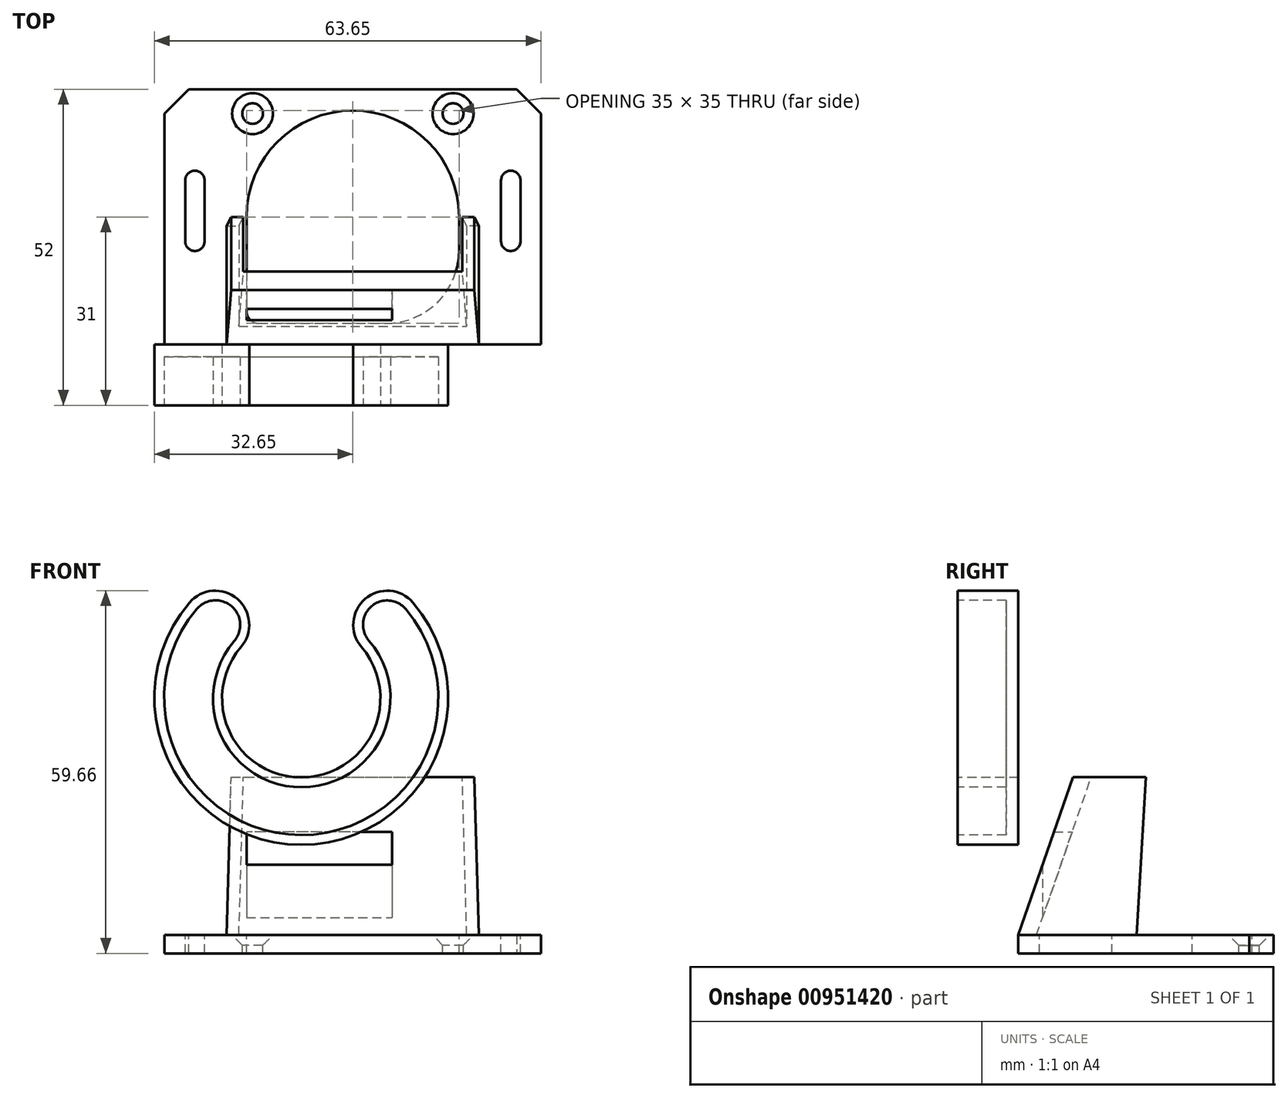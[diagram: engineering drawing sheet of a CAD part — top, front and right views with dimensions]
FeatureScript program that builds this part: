
annotation { "Feature Type Name" : "Feature", "Feature Type Description" : "" }
export const myFeature = defineFeature(function(context is Context, id is Id, definition is map)
    precondition{}
    {
        {
            var Q0;
            Q0=qCreatedBy(makeId("Top.planeOp"),FACE);
            var sketch = newSketch(context, id + "F0", { "sketchPlane" : qUnion([Q0])});
            skLineSegment(sketch, "E0.bottom", {"start": v(-31, 21) * mm, "end": v(31, 21) * mm});
            skLineSegment(sketch, "E0.top", {"start": v(-21, -21) * mm, "end": v(21.02, -21) * mm});
            skLineSegment(sketch, "E0.left", {"start": v(-31, 21) * mm, "end": v(-31, -9) * mm});
            skLineSegment(sketch, "E0.right", {"start": v(31, 21) * mm, "end": v(31, -9) * mm});
            skPoint(sketch, "E0.middle", {"position": v(0, 0) * mm});
            skLineSegment(sketch, "E1", {"start": v(-17.5, 0) * mm, "end": v(17.5, 0) * mm, "construction": true});
            skLineSegment(sketch, "E2.0", {"start": v(26, 21) * mm, "end": v(26, -21) * mm, "construction": true});
            skLineSegment(sketch, "E3.0", {"start": v(-26, 21) * mm, "end": v(-26, -21) * mm, "construction": true});
            skLineSegment(sketch, "E4.bottom", {"start": v(-27.6, -4) * mm, "end": v(-24.4, -4) * mm});
            skLineSegment(sketch, "E4.top", {"start": v(-27.6, 6) * mm, "end": v(-24.4, 6) * mm});
            skLineSegment(sketch, "E4.left", {"start": v(-27.6, -4) * mm, "end": v(-27.6, 6) * mm});
            skLineSegment(sketch, "E4.right", {"start": v(-24.4, -4) * mm, "end": v(-24.4, 6) * mm});
            skPoint(sketch, "E4.middle", {"position": v(-26, 1) * mm});
            skLineSegment(sketch, "E5.bottom", {"start": v(24.4, -4) * mm, "end": v(27.6, -4) * mm, "construction": true});
            skLineSegment(sketch, "E5.top", {"start": v(24.4, 6) * mm, "end": v(27.6, 6) * mm, "construction": true});
            skLineSegment(sketch, "E5.left", {"start": v(24.4, -4) * mm, "end": v(24.4, 6) * mm});
            skLineSegment(sketch, "E5.right", {"start": v(27.6, -4) * mm, "end": v(27.6, 6) * mm});
            skPoint(sketch, "E5.middle", {"position": v(26, 1) * mm});
            skArc(sketch, "E6", {"start": v(27.6, 6) * mm, "mid": v(26, 7.6) * mm, "end": v(24.4, 6) * mm});
            skArc(sketch, "E7", {"start": v(24.4, -4) * mm, "mid": v(26, -5.6) * mm, "end": v(27.6, -4) * mm});
            skArc(sketch, "E8", {"start": v(-27.6, -4) * mm, "mid": v(-26, -5.6) * mm, "end": v(-24.4, -4) * mm});
            skArc(sketch, "E9", {"start": v(-24.4, 6) * mm, "mid": v(-26, 7.6) * mm, "end": v(-27.6, 6) * mm});
            skLineSegment(sketch, "E10", {"start": v(31, -9) * mm, "end": v(21.02, -9) * mm});
            skLineSegment(sketch, "E11", {"start": v(-31, -9) * mm, "end": v(-21, -9) * mm});
            skLineSegment(sketch, "E12", {"start": v(-21, -9) * mm, "end": v(-21, -21) * mm});
            skLineSegment(sketch, "E13", {"start": v(21.02, -9) * mm, "end": v(21.02, -21) * mm});
            skPoint(sketch, "E14.orphan", {"position": v(-31, -21) * mm});
            skPoint(sketch, "E15.trimOffspring.end.orphan", {"position": v(31, -21) * mm});
            skPoint(sketch, "E16", {"position": v(-16.5, 17) * mm});
            skPoint(sketch, "E17", {"position": v(16.5, 17) * mm});
            skLineSegment(sketch, "E18", {"start": v(0, 28) * mm, "end": v(0, -24.83) * mm, "construction": true});
            skArc(sketch, "E19.trimOffspring", {"start": v(17.5, 0) * mm, "mid": v(0, 17.5) * mm, "end": v(-17.5, 0) * mm});
            skLineSegment(sketch, "E20", {"start": v(21.02, -21) * mm, "end": v(31, -21) * mm});
            skLineSegment(sketch, "E21", {"start": v(31, -21) * mm, "end": v(31, -9) * mm});
            skLineSegment(sketch, "E22", {"start": v(-31, -9) * mm, "end": v(-31, -21) * mm});
            skLineSegment(sketch, "E23", {"start": v(-31, -21) * mm, "end": v(-21, -21) * mm});
            skLineSegment(sketch, "E24", {"start": v(-17.5, 0) * mm, "end": v(-17.5, -15.5) * mm});
            skPoint(sketch, "E24.endSnap0", {"position": v(-1.48, -17.5) * mm});
            skLineSegment(sketch, "E25", {"start": v(-15.5, -17.5) * mm, "end": v(5.5, -17.5) * mm});
            skLineSegment(sketch, "E26", {"start": v(17.5, -5.5) * mm, "end": v(17.5, 0) * mm});
            skPoint(sketch, "E27.visualSharp", {"position": v(-17.5, -17.5) * mm});
            skArc(sketch, "E27.filletArc", {"start": v(-17.5, -15.5) * mm, "mid": v(-16.91, -16.91) * mm, "end": v(-15.5, -17.5) * mm});
            skPoint(sketch, "E28.visualSharp", {"position": v(17.5, -17.5) * mm});
            skArc(sketch, "E28.filletArc", {"start": v(5.5, -17.5) * mm, "mid": v(13.99, -13.99) * mm, "end": v(17.5, -5.5) * mm});
            skSolve(sketch);
        }
        {
            var Q0;
            Q0=makeQuery(id+"F0.imprint","IMPRINT",FACE,{"disambiguationData":[TD([[makeQuery(id+"F0.imprint","IMPRINT",EDGE,{"derivedFrom":sQuery(id+"F0.wireOp",EDGE,"zgBuKsxa-OEMX-4A7b-Va0U-zt6h8Rh99ESV")}),-1.0]])]});
            var Q1;
            Q1=makeQuery(id+"F0.imprint","IMPRINT",FACE,{"disambiguationData":[TD([[makeQuery(id+"F0.imprint","IMPRINT",EDGE,{"derivedFrom":sQuery(id+"F0.wireOp",EDGE,"E11")}),-1.0]])]});
            var Q2;
            Q2=makeQuery(id+"F0.imprint","IMPRINT",FACE,{"disambiguationData":[TD([[makeQuery(id+"F0.imprint","IMPRINT",EDGE,{"derivedFrom":sQuery(id+"F0.wireOp",EDGE,"E10")}),1.0]])]});
            var Q3;
            Q3=makeQuery(id+"F0.imprint","IMPRINT",FACE,{"disambiguationData":[TD([[makeQuery(id+"F0.imprint","IMPRINT",EDGE,{"derivedFrom":sQuery(id+"F0.wireOp",EDGE,"E0.bottom")}),-1.0]])]});
            extrude(context, id + "F1", {"entities" : qUnion([Q0, Q1, Q2, Q3]), "oppositeDirection" : true, "depth" : 3 * mm, "offsetDistance" : 25 * mm});
        }
        {
            var Q0;
            Q0=sQuery(id+"F0.wireOp",VERTEX,"E16");
            var Q1;
            Q1=sQuery(id+"F0.wireOp",VERTEX,"E17");
            var Q2;
            Q2=makeQuery(id+"F1.opExtrude","SWEPT_BODY",BODY,{"disambiguationData":[OSD([sQuery(id+"F0.wireOp",EDGE,"zgBuKsxa-OEMX-4A7b-Va0U-zt6h8Rh99ESV"),sQuery(id+"F0.wireOp",EDGE,"E0.bottom"),sQuery(id+"F0.wireOp",EDGE,"E0.top"),sQuery(id+"F0.wireOp",EDGE,"E0.left"),sQuery(id+"F0.wireOp",EDGE,"E0.right"),sQuery(id+"F0.wireOp",EDGE,"8023575a-cc51-4947-99a3-caa3ee00ee31.0"),sQuery(id+"F0.wireOp",EDGE,"259734f9-b8b1-401e-8cfd-9bb92d609301.0"),sQuery(id+"F0.wireOp",EDGE,"E4.left"),sQuery(id+"F0.wireOp",EDGE,"E4.right"),sQuery(id+"F0.wireOp",EDGE,"E5.left"),sQuery(id+"F0.wireOp",EDGE,"E5.right"),sQuery(id+"F0.wireOp",EDGE,"E6"),sQuery(id+"F0.wireOp",EDGE,"E7"),sQuery(id+"F0.wireOp",EDGE,"E8"),sQuery(id+"F0.wireOp",EDGE,"E9"),sQuery(id+"F0.wireOp",EDGE,"E10"),sQuery(id+"F0.wireOp",EDGE,"E11"),sQuery(id+"F0.wireOp",EDGE,"E12"),sQuery(id+"F0.wireOp",EDGE,"E13"),sQuery(id+"F0.wireOp",EDGE,"E19.trimOffspring")])]});
            hole(context, id + "F2", {"style" : HoleStyle.C_SINK, "endStyle" : HoleEndStyle.THROUGH, "standardTappedOrClearance" : lookupTablePath({ "fit" : "Normal", "standard" : "ISO", "size" : "M3", "type" : "Clearance" }), "standardBlindInLast" : lookupTablePath({ "fit" : "Normal", "standard" : "ISO", "engagement" : "75%", "pitch" : "0.5 mm", "size" : "M3", "type" : "Clearance & tapped" }), "holeDiameter" : 3.4 * mm, "cSinkDiameter" : 6.72 * mm, "cSinkAngle" : 90 * degree, "majorDiameter" : 5 * mm, "isTappedThrough" : true, "tappedDepth" : 12 * mm, "tapClearance" : 3, "locations" : qUnion([Q0, Q1]), "scope" : qUnion([Q2])});
        }
        {
            var Q0;
            Q0=makeQuery(id+"F1.opExtrude","SWEPT_EDGE",EDGE,{"disambiguationData":[OSD([sQuery(id+"F0.wireOp",EDGE,"E0.bottom"),sQuery(id+"F0.wireOp",EDGE,"E0.right")])]});
            var Q1;
            Q1=makeQuery(id+"F1.opExtrude","SWEPT_EDGE",EDGE,{"disambiguationData":[OSD([sQuery(id+"F0.wireOp",EDGE,"E0.bottom"),sQuery(id+"F0.wireOp",EDGE,"E0.left")])]});
            chamfer(context, id + "F3", {"entities" : qUnion([Q0, Q1]), "width" : 4 * mm, "tangentPropagation" : true});
        }
        {
            var Q0;
            Q0=makeQuery(id+"F1.opExtrude","CAP_FACE",FACE,{"disambiguationData":[OSD([sQuery(id+"F0.wireOp",EDGE,"zgBuKsxa-OEMX-4A7b-Va0U-zt6h8Rh99ESV"),sQuery(id+"F0.wireOp",EDGE,"E0.bottom"),sQuery(id+"F0.wireOp",EDGE,"E0.top"),sQuery(id+"F0.wireOp",EDGE,"E0.left"),sQuery(id+"F0.wireOp",EDGE,"E0.right"),sQuery(id+"F0.wireOp",EDGE,"8023575a-cc51-4947-99a3-caa3ee00ee31.0"),sQuery(id+"F0.wireOp",EDGE,"259734f9-b8b1-401e-8cfd-9bb92d609301.0"),sQuery(id+"F0.wireOp",EDGE,"E4.left"),sQuery(id+"F0.wireOp",EDGE,"E4.right"),sQuery(id+"F0.wireOp",EDGE,"E5.left"),sQuery(id+"F0.wireOp",EDGE,"E5.right"),sQuery(id+"F0.wireOp",EDGE,"E6"),sQuery(id+"F0.wireOp",EDGE,"E7"),sQuery(id+"F0.wireOp",EDGE,"E8"),sQuery(id+"F0.wireOp",EDGE,"E9"),sQuery(id+"F0.wireOp",EDGE,"E10"),sQuery(id+"F0.wireOp",EDGE,"E11"),sQuery(id+"F0.wireOp",EDGE,"E12"),sQuery(id+"F0.wireOp",EDGE,"E13"),sQuery(id+"F0.wireOp",EDGE,"E19.trimOffspring")])],"isStart":true});
            var sketch = newSketch(context, id + "F4", { "sketchPlane" : qUnion([Q0])});
            skLineSegment(sketch, "E29.0", {"start": v(-20.75, -1.5) * mm, "end": v(-20.75, -21) * mm});
            skLineSegment(sketch, "E30.0", {"start": v(-20.75, -21) * mm, "end": v(20.75, -21) * mm});
            skLineSegment(sketch, "E31.0", {"start": v(20.75, -1.5) * mm, "end": v(20.75, -21) * mm});
            skLineSegment(sketch, "E32.0", {"start": v(18.75, -1.5) * mm, "end": v(18.75, -18) * mm});
            skLineSegment(sketch, "E32.1", {"start": v(-18.75, -18) * mm, "end": v(18.75, -18) * mm});
            skLineSegment(sketch, "E32.2", {"start": v(-18.75, -1.5) * mm, "end": v(-18.75, -18) * mm});
            skLineSegment(sketch, "E33", {"start": v(-20.75, -1.5) * mm, "end": v(-18.75, -1.5) * mm});
            skLineSegment(sketch, "E34", {"start": v(20.75, -1.5) * mm, "end": v(18.75, -1.5) * mm});
            skLineSegment(sketch, "E35", {"start": v(0, 24.47) * mm, "end": v(0, -25.01) * mm, "construction": true});
            skSolve(sketch);
        }
        {
            var Q0;
            Q0=makeQuery(id+"F4.imprint","IMPRINT",FACE,{"disambiguationData":[TD([[makeQuery(id+"F4.imprint","IMPRINT",EDGE,{"derivedFrom":sQuery(id+"F4.wireOp",EDGE,"E32.0")}),-1.0]])]});
            cPlane(context, id + "F5", {"entities" : qUnion([Q0]), "cplaneType" : CPlaneType.OFFSET, "offset" : 26 * mm, "width" : 150 * mm, "height" : 150 * mm});
        }
        {
            var Q0;
            Q0=qCreatedBy(id+"F5.planeOp",FACE);
            var sketch = newSketch(context, id + "F6", { "sketchPlane" : qUnion([Q0])});
            skLineSegment(sketch, "E36", {"start": v(-20.02, -12) * mm, "end": v(-20.02, 0) * mm});
            skLineSegment(sketch, "E37", {"start": v(20.02, -12) * mm, "end": v(20.02, 0) * mm});
            skLineSegment(sketch, "E38", {"start": v(20.02, 0) * mm, "end": v(18.02, 0) * mm});
            skLineSegment(sketch, "E39", {"start": v(18.02, 0) * mm, "end": v(18.02, -9) * mm});
            skLineSegment(sketch, "E40", {"start": v(-20.02, 0) * mm, "end": v(-18.02, 0) * mm});
            skLineSegment(sketch, "E41", {"start": v(-18.02, 0) * mm, "end": v(-18.02, -9) * mm});
            skLineSegment(sketch, "E42", {"start": v(-18.02, -9) * mm, "end": v(18.02, -9) * mm});
            skLineSegment(sketch, "E43", {"start": v(-20.02, -12) * mm, "end": v(20.02, -12) * mm});
            skSolve(sketch);
        }
        {
            var Q1;
            Q1=qSketchRegion(id+"F4",true);
            var Q2;
            Q2=qSketchRegion(id+"F6",true);
            loft(context, id + "F7", {"operationType" : NewBodyOperationType.ADD, "sheetProfilesArray" : [{ "sheetProfileEntities" : qUnion([Q1]) }, { "sheetProfileEntities" : qUnion([Q2]) }]});
        }
        {
            var Q0;
            Q0=makeQuery(id+"F1.opExtrude","CAP_FACE",FACE,{"disambiguationData":[OSD([sQuery(id+"F0.wireOp",EDGE,"zgBuKsxa-OEMX-4A7b-Va0U-zt6h8Rh99ESV"),sQuery(id+"F0.wireOp",EDGE,"E0.bottom"),sQuery(id+"F0.wireOp",EDGE,"E0.top"),sQuery(id+"F0.wireOp",EDGE,"E0.left"),sQuery(id+"F0.wireOp",EDGE,"E0.right"),sQuery(id+"F0.wireOp",EDGE,"E4.left"),sQuery(id+"F0.wireOp",EDGE,"E4.right"),sQuery(id+"F0.wireOp",EDGE,"E5.left"),sQuery(id+"F0.wireOp",EDGE,"E5.right"),sQuery(id+"F0.wireOp",EDGE,"E6"),sQuery(id+"F0.wireOp",EDGE,"E7"),sQuery(id+"F0.wireOp",EDGE,"E8"),sQuery(id+"F0.wireOp",EDGE,"E9"),sQuery(id+"F0.wireOp",EDGE,"E19.trimOffspring"),sQuery(id+"F0.wireOp",EDGE,"E20"),sQuery(id+"F0.wireOp",EDGE,"E21"),sQuery(id+"F0.wireOp",EDGE,"E22"),sQuery(id+"F0.wireOp",EDGE,"E23")])],"isStart":true});
            cPlane(context, id + "F8", {"entities" : qUnion([Q0]), "cplaneType" : CPlaneType.OFFSET, "offset" : 2 * mm, "width" : 150 * mm, "height" : 150 * mm});
        }
        {
            var Q0;
            Q0=qCreatedBy(id+"F8.planeOp",FACE);
            var sketch = newSketch(context, id + "F9", { "sketchPlane" : qUnion([Q0])});
            skLineSegment(sketch, "E44.bottom", {"start": v(6.5, -17) * mm, "end": v(-17.5, -17) * mm});
            skLineSegment(sketch, "E44.top", {"start": v(6.5, -12) * mm, "end": v(-17.5, -12) * mm});
            skLineSegment(sketch, "E44.left", {"start": v(6.5, -17) * mm, "end": v(6.5, -12) * mm});
            skLineSegment(sketch, "E44.right", {"start": v(-17.5, -17) * mm, "end": v(-17.5, -12) * mm});
            skSolve(sketch);
        }
        {
            var Q0;
            Q0=makeQuery(id+"F9.imprint","IMPRINT",FACE,{"disambiguationData":[TD([[makeQuery(id+"F9.imprint","IMPRINT",EDGE,{"derivedFrom":sQuery(id+"F9.wireOp",EDGE,"E44.bottom")}),-1.0]])]});
            extrude(context, id + "F10", {"entities" : qUnion([Q0]), "operationType" : NewBodyOperationType.REMOVE, "depth" : 15 * mm, "offsetDistance" : 25 * mm});
        }
        {
            var Q0;
            Q0=makeQuery(id+"F7.opLoft","SWEPT_FACE",FACE,{"disambiguationData":[OSD([sQuery(id+"F0.wireOp",EDGE,"E0.top"),sQuery(id+"F0.wireOp",EDGE,"E20"),sQuery(id+"F0.wireOp",EDGE,"E23"),sQuery(id+"F4.wireOp",EDGE,"E29.0"),sQuery(id+"F4.wireOp",EDGE,"E30.0"),sQuery(id+"F4.wireOp",EDGE,"E31.0"),sQuery(id+"F6.wireOp",EDGE,"E36"),sQuery(id+"F6.wireOp",EDGE,"E37"),sQuery(id+"F6.wireOp",EDGE,"E43")])]});
            var sketch = newSketch(context, id + "F11", { "sketchPlane" : qUnion([Q0])});
            skLineSegment(sketch, "E45.0", {"start": v(6.5, 11.12) * mm, "end": v(-17.5, 11.12) * mm, "construction": true});
            skLineSegment(sketch, "E46.0", {"start": v(-17.5, 11.12) * mm, "end": v(-17.5, 5.36) * mm, "construction": true});
            skEllipse(sketch, "E47", {"center": v(-5.5, 8.24) * mm, "majorRadius": 13.18 * mm, "minorRadius": 6.7 * mm, "majorAxis": v(1, 0)});
            skPoint(sketch, "E47.centerSnap0", {"position": v(-17.5, 8.24) * mm});
            skPoint(sketch, "E47.centerSnap1", {"position": v(-5.5, 11.12) * mm});
            skFitSpline(sketch, "E48.0", {"points": [v(9.22, 13.3) * mm, v(9.31, 14.28) * mm, v(9.22, 15.25) * mm, v(8.85, 16.5) * mm, v(8.17, 17.62) * mm, v(7.25, 18.6) * mm, v(6.17, 19.52) * mm, v(4.6, 20.49) * mm, v(2.76, 21.26) * mm, v(1.14, 21.75) * mm, v(-0.54, 22.15) * mm, v(-2.3, 22.43) * mm, v(-4.12, 22.56) * mm, v(-5.5, 22.6) * mm, v(-6.88, 22.56) * mm, v(-8.7, 22.43) * mm, v(-10.46, 22.15) * mm, v(-12.14, 21.75) * mm, v(-13.76, 21.26) * mm, v(-15.6, 20.49) * mm, v(-17.17, 19.52) * mm, v(-18.25, 18.6) * mm, v(-19.17, 17.62) * mm, v(-19.85, 16.5) * mm, v(-20.22, 15.25) * mm, v(-20.31, 14.28) * mm, v(-20.22, 13.3) * mm, v(-19.85, 12.06) * mm, v(-19.17, 10.94) * mm, v(-18.25, 9.95) * mm, v(-17.17, 9.04) * mm, v(-15.6, 8.07) * mm, v(-13.76, 7.3) * mm, v(-12.14, 6.8) * mm, v(-10.46, 6.4) * mm, v(-8.7, 6.13) * mm, v(-6.88, 6) * mm, v(-5.5, 5.96) * mm, v(-4.12, 6) * mm, v(-2.3, 6.13) * mm, v(-0.54, 6.4) * mm, v(1.14, 6.8) * mm, v(2.76, 7.3) * mm, v(4.6, 8.07) * mm, v(6.17, 9.04) * mm, v(7.25, 9.95) * mm, v(8.17, 10.94) * mm, v(8.85, 12.06) * mm, v(9.22, 13.3) * mm, v(9.31, 14.28) * mm, v(9.22, 15.25) * mm, v(9.22, 13.3) * mm]});
            skSolve(sketch);
        }
        {
            var Q0;
            {var subQ0=sQuery(id+"F0.wireOp",EDGE,"E23");var subQ1=sQuery(id+"F0.wireOp",EDGE,"E20");var subQ2=sQuery(id+"F0.wireOp",EDGE,"E0.top");Q0=makeQuery(id+"FMINiw3eGN9fXnE_1.boolean.opBoolean","SPLIT",FACE,{"disambiguationData":[TD([makeQuery(id+"FMINiw3eGN9fXnE_1.opExtrude","SWEPT_FACE",FACE,{"disambiguationData":[OSD([sQuery(id+"Far563bkZVvMWru_1.wireOp",EDGE,"df4eb139-c0bc-4f98-82ec-923183797030.0")])]})])],"derivedFrom":makeQuery(id+"F1.opExtrude","SWEPT_FACE",FACE,{"disambiguationData":[OSD([subQ2,subQ1,subQ0])]})});}
            cPlane(context, id + "F12", {"entities" : qUnion([Q0]), "cplaneType" : CPlaneType.OFFSET, "offset" : 10 * mm, "width" : 150 * mm, "height" : 150 * mm});
        }
        {
            var Q0;
            Q0=qCreatedBy(id+"F12.planeOp",FACE);
            var sketch = newSketch(context, id + "F13", { "sketchPlane" : qUnion([Q0])});
            skLineSegment(sketch, "E49.0", {"start": v(13.92, 49) * mm, "end": v(11.52, 49) * mm, "construction": true});
            skLineSegment(sketch, "E49.1", {"start": v(13.92, 49) * mm, "end": v(13.92, 25.6) * mm, "construction": true});
            skLineSegment(sketch, "E49.4", {"start": v(-24.88, 49) * mm, "end": v(-24.88, 25.6) * mm, "construction": true});
            skLineSegment(sketch, "E49.5", {"start": v(10.52, 50) * mm, "end": v(10.52, 29) * mm, "construction": true});
            skLineSegment(sketch, "E49.7", {"start": v(10.52, 29) * mm, "end": v(-21.48, 29) * mm, "construction": true});
            skLineSegment(sketch, "E49.9", {"start": v(-21.48, 50) * mm, "end": v(-21.48, 29) * mm, "construction": true});
            skLineSegment(sketch, "E49.10", {"start": v(-22.48, 49) * mm, "end": v(-24.88, 49) * mm, "construction": true});
            skPoint(sketch, "E50.visualSharp", {"position": v(13.92, 25.6) * mm});
            skLineSegment(sketch, "E51", {"start": v(-21.48, 49) * mm, "end": v(10.52, 49) * mm, "construction": true});
            skLineSegment(sketch, "E52.0", {"start": v(-20.75, 0) * mm, "end": v(-20.03, 25.6) * mm, "construction": true});
            skLineSegment(sketch, "E53.0", {"start": v(-20.75, 0) * mm, "end": v(20.75, 0) * mm, "construction": true});
            skLineSegment(sketch, "E54.0", {"start": v(-21.48, 39) * mm, "end": v(4.52, 39) * mm, "construction": true});
            skLineSegment(sketch, "E55.0", {"start": v(-24.88, 25.6) * mm, "end": v(13.92, 25.6) * mm, "construction": true});
            skLineSegment(sketch, "E56.1", {"start": v(14.92, 50) * mm, "end": v(14.92, 24.6) * mm, "construction": true});
            skLineSegment(sketch, "E56.3", {"start": v(-25.88, 50) * mm, "end": v(-25.88, 24.6) * mm, "construction": true});
            skLineSegment(sketch, "E57.0", {"start": v(11.52, 49) * mm, "end": v(11.52, 28) * mm, "construction": true});
            skLineSegment(sketch, "E57.1", {"start": v(11.52, 28) * mm, "end": v(-22.48, 28) * mm, "construction": true});
            skLineSegment(sketch, "E57.3", {"start": v(-22.48, 49) * mm, "end": v(-22.48, 28) * mm, "construction": true});
            skLineSegment(sketch, "E58", {"start": v(-25.88, 24.6) * mm, "end": v(14.92, 24.6) * mm, "construction": true});
            skArc(sketch, "E59.0", {"start": v(-25.68, 53.66) * mm, "mid": v(-8.48, 16.47) * mm, "end": v(8.7, 53.66) * mm});
            skArc(sketch, "E60.0", {"start": v(-26.9, 54.7) * mm, "mid": v(-8.48, 14.87) * mm, "end": v(9.93, 54.7) * mm});
            skLineSegment(sketch, "E61", {"start": v(-8.48, 39) * mm, "end": v(-27.8, 55.47) * mm, "construction": true});
            skLineSegment(sketch, "E62", {"start": v(-8.48, 66.2) * mm, "end": v(-8.48, 39) * mm, "construction": true});
            skLineSegment(sketch, "E63.MirrorCS", {"start": v(-8.48, 39) * mm, "end": v(10.84, 55.47) * mm, "construction": true});
            skArc(sketch, "E64.trimOffspring", {"start": v(-18.38, 47.44) * mm, "mid": v(-8.48, 25.93) * mm, "end": v(1.42, 47.44) * mm});
            skArc(sketch, "E65.trimOffspring", {"start": v(-19.5, 48.4) * mm, "mid": v(-8.35, 24.32) * mm, "end": v(2.63, 48.48) * mm});
            skArc(sketch, "E66", {"start": v(-18.38, 47.44) * mm, "mid": v(-19.01, 55.32) * mm, "end": v(-26.9, 54.7) * mm});
            skArc(sketch, "E67.MirrorCS", {"start": v(1.42, 47.44) * mm, "mid": v(2.04, 55.32) * mm, "end": v(9.93, 54.7) * mm});
            skArc(sketch, "E68.trimOffspring", {"start": v(-19.5, 48.4) * mm, "mid": v(-19.96, 54.11) * mm, "end": v(-25.68, 53.66) * mm});
            skArc(sketch, "E69", {"start": v(8.74, 53.62) * mm, "mid": v(3.08, 54.1) * mm, "end": v(2.67, 48.44) * mm});
            skPoint(sketch, "E70.0", {"position": v(-5.5, 14.28) * mm});
            skSolve(sketch);
        }
        {
            var Q0;
            Q0=qCreatedBy(makeId("Right.planeOp"),FACE);
            cPlane(context, id + "F14", {"entities" : qUnion([Q0]), "cplaneType" : CPlaneType.OFFSET, "offset" : 5.5 * mm, "oppositeDirection" : true, "width" : 150 * mm, "height" : 150 * mm});
        }
        {
            var Q0;
            {var subQ1=sQuery(id+"F13.wireOp",EDGE,"E59.0");Q0=makeQuery(id+"F13.imprint","IMPRINT",FACE,{"disambiguationData":[TD([[makeQuery(id+"F13.imprint","IMPRINT",EDGE,{"derivedFrom":subQ1}),-1.0]])]});}
            extrude(context, id + "F15", {"entities" : qUnion([Q0]), "oppositeDirection" : true, "depth" : 8 * mm, "offsetDistance" : 25 * mm});
        }
        {
            var Q0;
            Q0=makeQuery(id+"F15.opExtrude","CAP_FACE",FACE,{"disambiguationData":[OSD([sQuery(id+"F13.wireOp",EDGE,"E59.0"),sQuery(id+"F13.wireOp",EDGE,"E60.0"),sQuery(id+"F13.wireOp",EDGE,"E64.trimOffspring"),sQuery(id+"F13.wireOp",EDGE,"E65.trimOffspring"),sQuery(id+"F13.wireOp",EDGE,"E66"),sQuery(id+"F13.wireOp",EDGE,"E67.MirrorCS"),sQuery(id+"F13.wireOp",EDGE,"E68.trimOffspring"),sQuery(id+"F13.wireOp",EDGE,"E69")])],"isStart":false});
            var sketch = newSketch(context, id + "F16", { "sketchPlane" : qUnion([Q0])});
            skArc(sketch, "E71.0.0", {"start": v(18.38, 47.44) * mm, "mid": v(8.48, 25.93) * mm, "end": v(-1.42, 47.44) * mm});
            skArc(sketch, "E71.0.1", {"start": v(-1.42, 47.44) * mm, "mid": v(-2.04, 55.32) * mm, "end": v(-9.93, 54.7) * mm});
            skArc(sketch, "E71.0.2", {"start": v(-9.93, 54.7) * mm, "mid": v(8.48, 14.87) * mm, "end": v(26.9, 54.7) * mm});
            skArc(sketch, "E71.0.3", {"start": v(26.9, 54.7) * mm, "mid": v(19.01, 55.32) * mm, "end": v(18.38, 47.44) * mm});
            skSolve(sketch);
        }
        {
            var Q0;
            Q0 = qSketchRegion(id + "F16", true);
            extrude(context, id + "F17", {"entities" : qUnion([Q0]), "operationType" : NewBodyOperationType.ADD, "depth" : 2 * mm, "offsetDistance" : 25 * mm});
        }
    });
